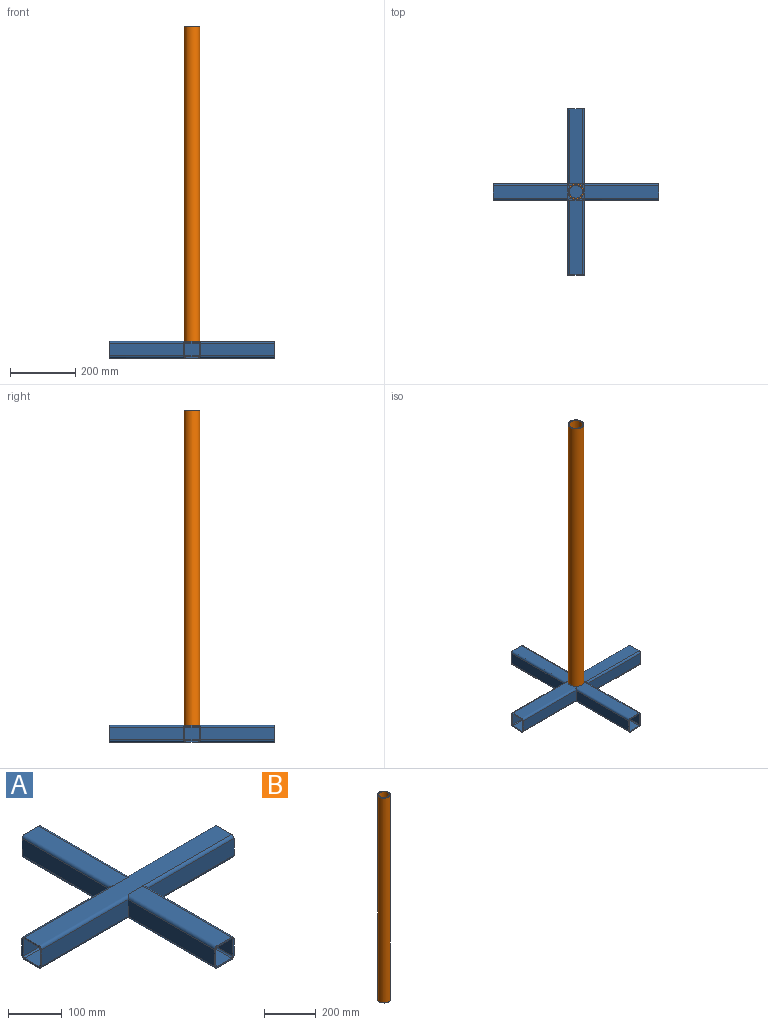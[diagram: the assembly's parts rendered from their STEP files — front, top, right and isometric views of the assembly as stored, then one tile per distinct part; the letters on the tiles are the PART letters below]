
ASSEMBLY  parts=2 mates=1
PART A: 104 faces, bbox 508x508x50.8 mm
  f0: plane 228.6x38.1mm, normal (0,-1,0), area 8709.7mm2, adj f3,f11,f28,f45
  f1: plane 228.6x38.1mm, normal (0,-1,0), area 8709.7mm2, adj f2,f10,f29,f44
  f2: cylinder r=6.35mm len=273.05mm, axis (1,0,0), area 2303.2mm2, adj f1,f26,f29,f41,f42,f43,f81
  f3: cylinder r=6.35mm len=234.95mm, axis (1,0,0), area 2303.2mm2, adj f0,f26,f28,f43,f81
  f4: cylinder r=6.35mm len=273.05mm, axis (1,0,0), area 2303.2mm2, adj f6,f26,f28,f64,f65,f66,f80
  f5: cylinder r=6.35mm len=234.95mm, axis (1,0,0), area 2303.2mm2, adj f7,f26,f29,f64,f80
  f6: plane 228.6x38.1mm, normal (0,1,0), area 8709.7mm2, adj f4,f9,f28,f63
  f7: plane 228.6x38.1mm, normal (0,1,0), area 8709.7mm2, adj f5,f8,f29,f62
  f8: cylinder r=6.35mm len=234.95mm, axis (1,0,0), area 2303.2mm2, adj f7,f27,f29,f61,f79
  f9: cylinder r=6.35mm len=273.05mm, axis (1,0,0), area 2303.2mm2, adj f6,f27,f28,f59,f60,f61,f79
  f10: cylinder r=6.35mm len=273.05mm, axis (1,0,0), area 2303.2mm2, adj f1,f27,f29,f38,f39,f40,f58
  f11: cylinder r=6.35mm len=234.95mm, axis (1,0,0), area 2303.2mm2, adj f0,f27,f28,f38,f58
  f12: cylinder r=3.17mm len=229.45mm, axis (1,0,0), area 1142.2mm2, adj f25,f29,f30,f34
  f13: cylinder r=3.17mm len=229.45mm, axis (1,0,0), area 1142.2mm2, adj f14,f24,f28,f37
  f14: plane 229.45x38.1mm, normal (0,0,1), area 8742.1mm2, adj f13,f16,f28,f37
  f15: cylinder r=3.17mm len=229.45mm, axis (1,0,0), area 1142.2mm2, adj f18,f29,f30,f34
  f16: cylinder r=3.17mm len=229.45mm, axis (1,0,0), area 1142.2mm2, adj f14,f17,f28,f37
  f17: plane 228.6x38.1mm, normal (0,1,0), area 8709.7mm2, adj f16,f19,f28,f35
  f18: plane 228.6x38.1mm, normal (0,1,0), area 8709.7mm2, adj f15,f20,f29,f32
  f19: cylinder r=3.17mm len=229.45mm, axis (1,0,0), area 1142.2mm2, adj f17,f28,f31,f36
  f20: cylinder r=3.17mm len=229.45mm, axis (1,0,0), area 1142.2mm2, adj f18,f21,f29,f33
  f21: plane 229.45x38.1mm, normal (0,0,-1), area 8742.1mm2, adj f20,f23,f29,f33
  f22: cylinder r=3.17mm len=229.45mm, axis (1,0,0), area 1142.2mm2, adj f24,f28,f31,f36
  f23: cylinder r=3.17mm len=229.45mm, axis (1,0,0), area 1142.2mm2, adj f21,f25,f29,f33
  f24: plane 228.6x38.1mm, normal (0,-1,0), area 8709.7mm2, adj f13,f22,f28,f35
  f25: plane 228.6x38.1mm, normal (0,-1,0), area 8709.7mm2, adj f12,f23,f29,f32
  f26: plane 508x38.1mm, normal (0,0,-1), area 19354.8mm2, adj f2,f3,f4,f5,f28,f29,f80,f81
  f27: plane 508x38.1mm, normal (0,0,1), area 19354.8mm2, adj f8,f9,f10,f11,f28,f29,f58,f79
  f28: plane 50.8x50.8mm, normal (-1,0,0), area 578.9mm2, adj f0,f3,f4,f6,f9,f11,f13,f14
  f29: plane 50.8x50.8mm, normal (1,0,0), area 578.9mm2, adj f1,f2,f5,f7,f8,f10,f12,f15
  f30: plane 229.45x38.1mm, normal (0,0,1), area 8742.1mm2, adj f12,f15,f29,f34
  f31: plane 229.45x38.1mm, normal (0,0,-1), area 8742.1mm2, adj f19,f22,f28,f36
  f32: plane 44.45x38.1mm, normal (1,0,0), area 1693.5mm2, adj f18,f25,f33,f34
  f33: cylinder r=6.35mm len=44.45mm, axis (0,-1,0), area 143.1mm2, adj f20,f21,f23,f32
  f34: cylinder r=6.35mm len=44.45mm, axis (0,-1,0), area 143.1mm2, adj f12,f15,f30,f32
  f35: plane 44.45x38.1mm, normal (-1,0,0), area 1693.5mm2, adj f17,f24,f36,f37
  f36: cylinder r=6.35mm len=44.45mm, axis (0,-1,0), area 143.1mm2, adj f19,f22,f31,f35
  f37: cylinder r=6.35mm len=44.45mm, axis (0,-1,0), area 143.1mm2, adj f13,f14,f16,f35
  f38: cylinder r=6.35mm len=234.95mm, axis (0,-1,0), area 2303.2mm2, adj f10,f11,f39,f45,f46
  f39: plane 234.95x38.1mm, normal (0,0,1), area 8951.6mm2, adj f10,f38,f40,f46
  f40: cylinder r=6.35mm len=234.95mm, axis (0,-1,0), area 2303.2mm2, adj f10,f39,f44,f46
  f41: cylinder r=6.35mm len=234.95mm, axis (0,-1,0), area 2303.2mm2, adj f2,f42,f44,f46
  f42: plane 234.95x38.1mm, normal (0,0,-1), area 8951.6mm2, adj f2,f41,f43,f46
  f43: cylinder r=6.35mm len=234.95mm, axis (0,-1,0), area 2303.2mm2, adj f2,f3,f42,f45,f46
  f44: plane 228.6x38.1mm, normal (1,0,0), area 8709.7mm2, adj f1,f40,f41,f46
  f45: plane 228.6x38.1mm, normal (-1,0,0), area 8709.7mm2, adj f0,f38,f43,f46
  f46: plane 50.8x50.8mm, normal (0,-1,0), area 578.9mm2, adj f38,f39,f40,f41,f42,f43,f44,f45
  f47: cylinder r=3.17mm len=229.45mm, axis (0,-1,0), area 1142.2mm2, adj f46,f48,f54,f56
  f48: plane 229.45x38.1mm, normal (0,0,1), area 8742.1mm2, adj f46,f47,f49,f56
  f49: cylinder r=3.17mm len=229.45mm, axis (0,-1,0), area 1142.2mm2, adj f46,f48,f53,f56
  f50: cylinder r=3.17mm len=229.45mm, axis (0,-1,0), area 1142.2mm2, adj f46,f51,f53,f55
  f51: plane 229.45x38.1mm, normal (0,0,-1), area 8742.1mm2, adj f46,f50,f52,f55
  f52: cylinder r=3.17mm len=229.45mm, axis (0,-1,0), area 1142.2mm2, adj f46,f51,f54,f55
  f53: plane 228.6x38.1mm, normal (-1,0,0), area 8709.7mm2, adj f46,f49,f50,f57
  f54: plane 228.6x38.1mm, normal (1,0,0), area 8709.7mm2, adj f46,f47,f52,f57
  f55: cylinder r=6.35mm len=44.45mm, axis (1,0,0), area 143.1mm2, adj f50,f51,f52,f57
  f56: cylinder r=6.35mm len=44.45mm, axis (1,0,0), area 143.1mm2, adj f47,f48,f49,f57
  f57: plane 44.45x38.1mm, normal (0,-1,0), area 1693.5mm2, adj f53,f54,f55,f56
  f58: cylinder r=6.35mm len=0mm, axis (0,-1,0), area 0mm2, adj f10,f11,f27
  f59: cylinder r=6.35mm len=234.95mm, axis (0,-1,0), area 2303.2mm2, adj f9,f60,f63,f67
  f60: plane 234.95x38.1mm, normal (0,0,1), area 8951.6mm2, adj f9,f59,f61,f67
  f61: cylinder r=6.35mm len=234.95mm, axis (0,-1,0), area 2303.2mm2, adj f8,f9,f60,f62,f67
  f62: plane 228.6x38.1mm, normal (1,0,0), area 8709.7mm2, adj f7,f61,f64,f67
  f63: plane 228.6x38.1mm, normal (-1,0,0), area 8709.7mm2, adj f6,f59,f66,f67
  f64: cylinder r=6.35mm len=234.95mm, axis (0,-1,0), area 2303.2mm2, adj f4,f5,f62,f65,f67
  f65: plane 234.95x38.1mm, normal (0,0,-1), area 8951.6mm2, adj f4,f64,f66,f67
  f66: cylinder r=6.35mm len=234.95mm, axis (0,-1,0), area 2303.2mm2, adj f4,f63,f65,f67
  f67: plane 50.8x50.8mm, normal (0,1,0), area 578.9mm2, adj f59,f60,f61,f62,f63,f64,f65,f66
  f68: cylinder r=3.17mm len=229.45mm, axis (0,-1,0), area 1142.2mm2, adj f67,f69,f71,f76
  f69: plane 229.45x38.1mm, normal (0,0,-1), area 8742.1mm2, adj f67,f68,f70,f76
  f70: cylinder r=3.17mm len=229.45mm, axis (0,-1,0), area 1142.2mm2, adj f67,f69,f72,f76
  f71: plane 228.6x38.1mm, normal (-1,0,0), area 8709.7mm2, adj f67,f68,f75,f77
  f72: plane 228.6x38.1mm, normal (1,0,0), area 8709.7mm2, adj f67,f70,f73,f77
  f73: cylinder r=3.17mm len=229.45mm, axis (0,-1,0), area 1142.2mm2, adj f67,f72,f74,f78
  f74: plane 229.45x38.1mm, normal (0,0,1), area 8742.1mm2, adj f67,f73,f75,f78
  f75: cylinder r=3.17mm len=229.45mm, axis (0,-1,0), area 1142.2mm2, adj f67,f71,f74,f78
  f76: cylinder r=6.35mm len=44.45mm, axis (1,0,0), area 143.1mm2, adj f68,f69,f70,f77
  f77: plane 44.45x38.1mm, normal (0,1,0), area 1693.5mm2, adj f71,f72,f76,f78
  f78: cylinder r=6.35mm len=44.45mm, axis (1,0,0), area 143.1mm2, adj f73,f74,f75,f77
  f79: cylinder r=6.35mm len=0mm, axis (0,-1,0), area 0mm2, adj f8,f9,f27
  f80: cylinder r=6.35mm len=0mm, axis (0,-1,0), area 0mm2, adj f4,f5,f26
  f81: cylinder r=6.35mm len=0mm, axis (0,-1,0), area 0mm2, adj f2,f3,f26
  f82: plane 44.45x38.1mm, normal (-1,0,0), area 1693.5mm2, adj f83,f84,f87,f90
  f83: cylinder r=3.17mm len=44.45mm, axis (0,-1,0), area 210.2mm2, adj f82,f89,f91,f92,f93
  f84: cylinder r=3.17mm len=44.45mm, axis (0,-1,0), area 210.2mm2, adj f82,f85,f86,f95,f96
  f85: cylinder r=3.17mm len=44.45mm, axis (1,0,0), area 210.2mm2, adj f84,f87,f95,f99,f102
  f86: cylinder r=3.17mm len=0mm, axis (1,0,0), area 0mm2, adj f84,f95,f103
  f87: plane 44.45x38.1mm, normal (0,1,0), area 1693.5mm2, adj f82,f85,f93,f97
  f88: cylinder r=3.17mm len=0mm, axis (1,0,0), area 0mm2, adj f92,f98,f101
  f89: cylinder r=3.17mm len=44.45mm, axis (1,0,0), area 210.2mm2, adj f83,f90,f92,f98,f100
  f90: plane 44.45x38.1mm, normal (0,-1,0), area 1693.5mm2, adj f82,f89,f96,f97
  f91: cylinder r=3.17mm len=0mm, axis (1,0,0), area 0mm2, adj f83,f92,f100
  f92: plane 38.1x38.1mm, normal (0,0,-1), area 1451.6mm2, adj f83,f88,f89,f91,f93,f98
  f93: cylinder r=3.17mm len=44.45mm, axis (1,0,0), area 210.2mm2, adj f83,f87,f92,f98,f101
  f94: cylinder r=3.17mm len=0mm, axis (1,0,0), area 0mm2, adj f95,f99,f102
  f95: plane 38.1x38.1mm, normal (0,0,1), area 1451.6mm2, adj f84,f85,f86,f94,f96,f99
  f96: cylinder r=3.17mm len=44.45mm, axis (1,0,0), area 210.2mm2, adj f84,f90,f95,f99,f103
  f97: plane 44.45x38.1mm, normal (1,0,0), area 1693.5mm2, adj f87,f90,f98,f99
  f98: cylinder r=3.17mm len=44.45mm, axis (0,-1,0), area 210.2mm2, adj f88,f89,f92,f93,f97
  f99: cylinder r=3.17mm len=44.45mm, axis (0,-1,0), area 210.2mm2, adj f85,f94,f95,f96,f97
  f100: cylinder r=3.17mm len=0mm, axis (0,-1,0), area 0mm2, adj f89,f91
  f101: cylinder r=3.17mm len=0mm, axis (0,-1,0), area 0mm2, adj f88,f93
  f102: cylinder r=3.17mm len=0mm, axis (0,-1,0), area 0mm2, adj f85,f94
  f103: cylinder r=3.17mm len=0mm, axis (0,-1,0), area 0mm2, adj f86,f96
PART B: 4 faces, bbox 48.3x48.3x965.2 mm
  f0: cylinder r=20.45mm len=965.2mm, axis (0,0,1), area 124001.5mm2, adj f1,f2
  f1: plane 48.26x48.26mm, normal (0,0,-1), area 515.8mm2, adj f0,f3
  f2: plane 48.26x48.26mm, normal (0,0,1), area 515.8mm2, adj f0,f3
  f3: cylinder r=24.13mm len=965.2mm, axis (0,0,1), area 146337.1mm2, adj f1,f2
PLACE A t=(-0.55,3.38,25.36)mm fixed
PLACE B t=(-0.55,3.38,-219.78)mm
MATE fastened A.f27 <-> B.f0  axis (0,0,1) through (-0.55,3.38,50.76)mm
